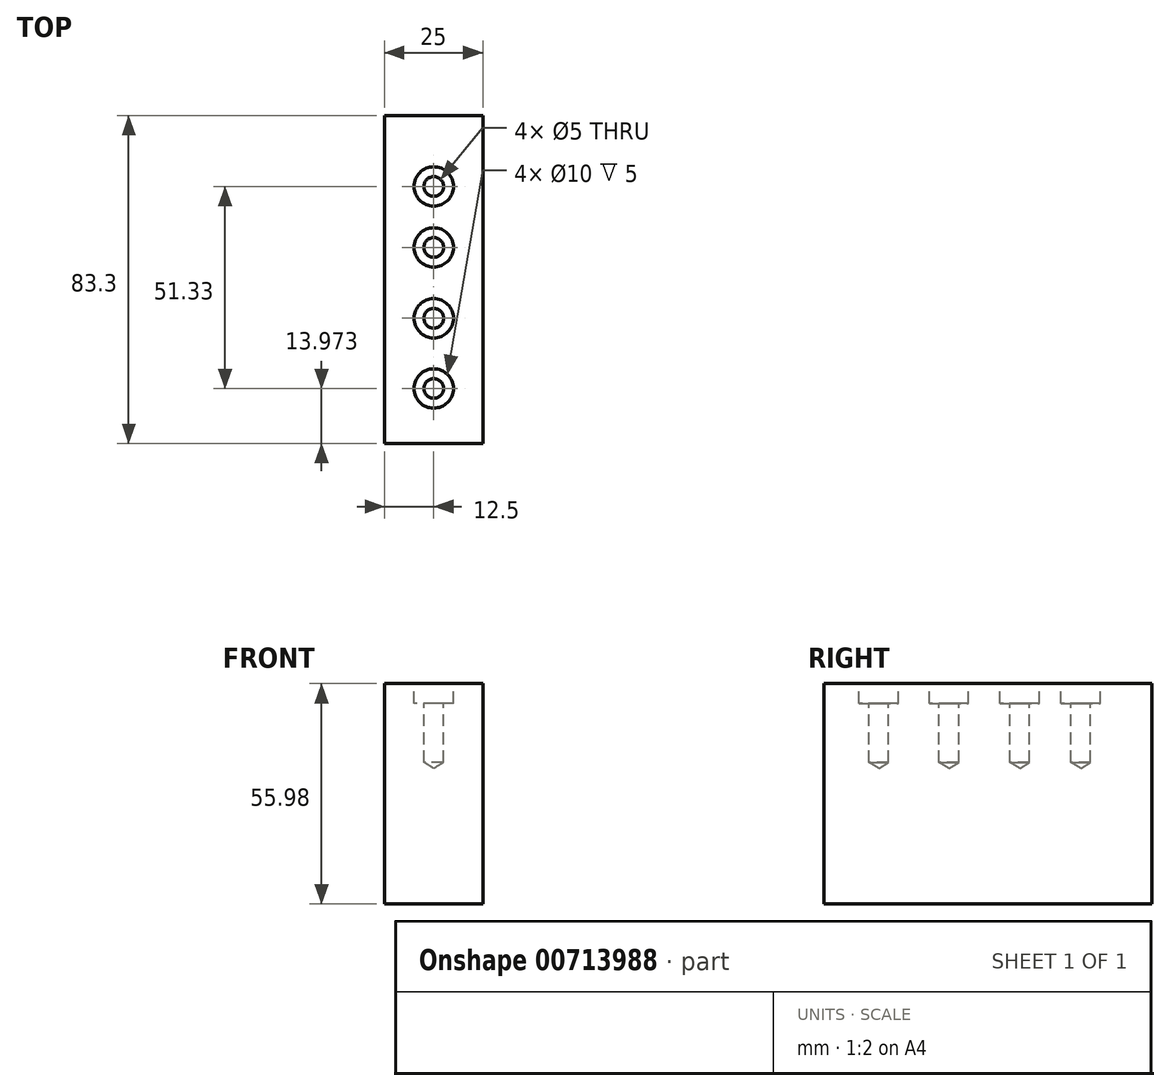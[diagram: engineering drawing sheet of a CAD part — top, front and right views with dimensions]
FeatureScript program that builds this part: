
annotation { "Feature Type Name" : "Feature", "Feature Type Description" : "" }
export const myFeature = defineFeature(function(context is Context, id is Id, definition is map)
    precondition{}
    {
        {
            var Q0;
            Q0=qCreatedBy(makeId("Right.planeOp"),FACE);
            var sketch = newSketch(context, id + "F0", { "sketchPlane" : qUnion([Q0])});
            skLineSegment(sketch, "E0.rect.bottom", {"start": v(-41.65, 27.99) * mm, "end": v(41.65, 27.99) * mm});
            skLineSegment(sketch, "E0.rect.top", {"start": v(-41.65, -27.99) * mm, "end": v(41.65, -27.99) * mm});
            skLineSegment(sketch, "E0.rect.left", {"start": v(-41.65, 27.99) * mm, "end": v(-41.65, -27.99) * mm});
            skLineSegment(sketch, "E0.rect.right", {"start": v(41.65, 27.99) * mm, "end": v(41.65, -27.99) * mm});
            skPoint(sketch, "E0.rect.middle", {"position": v(0, 0) * mm});
            skSolve(sketch);
        }
        {
            var Q0;
            Q0=qSketchRegion(id+"F0",true);
            extrude(context, id + "F1", {"entities" : qUnion([Q0]), "depth" : 25 * mm});
        }
        {
            var Q0;
            Q0=makeQuery(id+"F1.opExtrude","SWEPT_FACE",FACE,{"disambiguationData":[OSD([sQuery(id+"F0.wireOp",EDGE,"E0.rect.bottom")])]});
            var sketch = newSketch(context, id + "F2", { "sketchPlane" : qUnion([Q0])});
            skPoint(sketch, "E1", {"position": v(12.5, -27.68) * mm});
            skPoint(sketch, "E2", {"position": v(12.5, -9.83) * mm});
            skPoint(sketch, "E3", {"position": v(12.5, 23.65) * mm});
            skLineSegment(sketch, "E4", {"start": v(12.5, -41.65) * mm, "end": v(12.5, 41.65) * mm, "construction": true});
            skPoint(sketch, "E5", {"position": v(12.5, 8.16) * mm});
            skSolve(sketch);
        }
        {
            var Q0;
            Q0=sQuery(id+"F2.wireOp",VERTEX,"E1");
            var Q1;
            Q1=sQuery(id+"F2.wireOp",VERTEX,"E2");
            var Q2;
            Q2=sQuery(id+"F2.wireOp",VERTEX,"E5");
            var Q3;
            Q3=sQuery(id+"F2.wireOp",VERTEX,"E3");
            var Q4;
            Q4=makeQuery(id+"F1.opExtrude","SWEPT_BODY",BODY,{"disambiguationData":[OSD([sQuery(id+"F0.wireOp",EDGE,"E0.rect.bottom"),sQuery(id+"F0.wireOp",EDGE,"E0.rect.top"),sQuery(id+"F0.wireOp",EDGE,"E0.rect.left"),sQuery(id+"F0.wireOp",EDGE,"E0.rect.right")])]});
            hole(context, id + "F3", {"style" : HoleStyle.C_BORE, "holeDiameter" : 5 * mm, "cBoreDiameter" : 10 * mm, "cBoreDepth" : 5 * mm, "endStyle" : HoleEndStyle.BLIND, "holeDepth" : 20 * mm, "locations" : qUnion([Q0, Q1, Q2, Q3]), "scope" : qUnion([Q4])});
        }
        {
            var Q0;
            Q0=makeQuery(id+"F1.opExtrude","CAP_FACE",FACE,{"disambiguationData":[OSD([sQuery(id+"F0.wireOp",EDGE,"E0.rect.bottom"),sQuery(id+"F0.wireOp",EDGE,"E0.rect.top"),sQuery(id+"F0.wireOp",EDGE,"E0.rect.left"),sQuery(id+"F0.wireOp",EDGE,"E0.rect.right")])],"isStart":false});
            var sketch = newSketch(context, id + "F4", { "sketchPlane" : qUnion([Q0])});
            skLineSegment(sketch, "E6.0.0", {"start": v(41.65, 27.99) * mm, "end": v(-41.65, 27.99) * mm});
            skLineSegment(sketch, "E6.0.1", {"start": v(-41.65, 27.99) * mm, "end": v(-41.65, -27.99) * mm});
            skLineSegment(sketch, "E6.0.2", {"start": v(-41.65, -27.99) * mm, "end": v(41.65, -27.99) * mm});
            skLineSegment(sketch, "E6.0.3", {"start": v(41.65, -27.99) * mm, "end": v(41.65, 27.99) * mm});
            skSolve(sketch);
        }
    });
